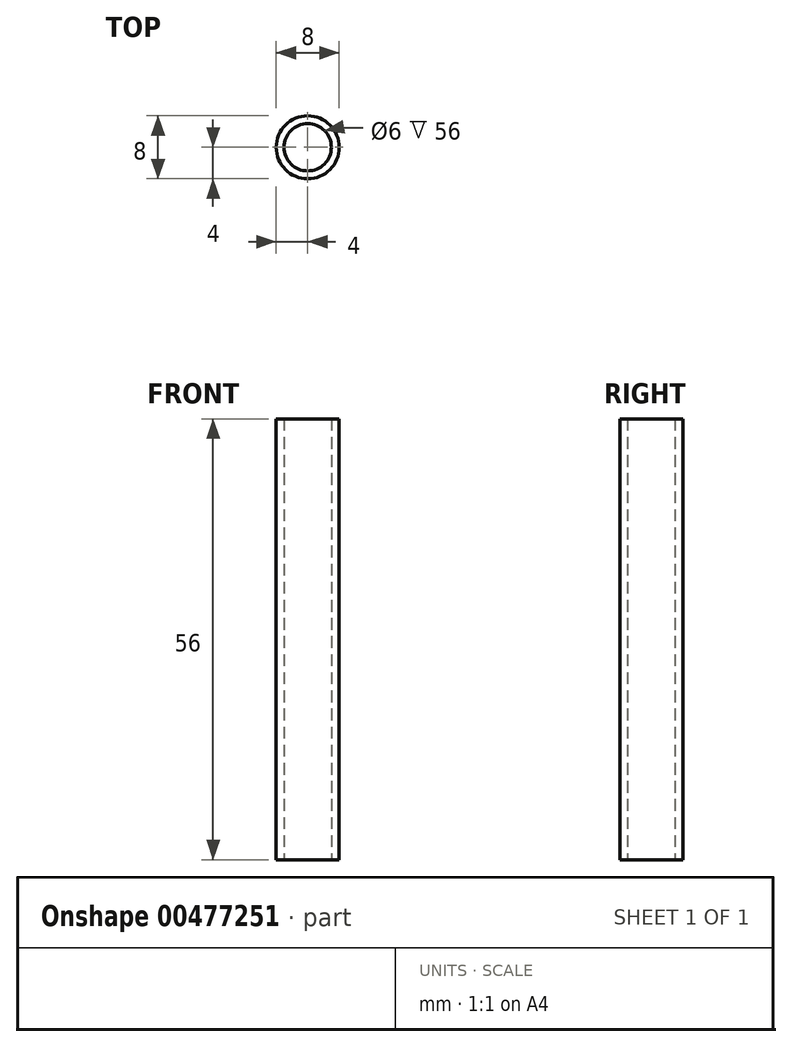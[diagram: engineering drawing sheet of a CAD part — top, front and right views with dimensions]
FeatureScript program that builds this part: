
annotation { "Feature Type Name" : "Feature", "Feature Type Description" : "" }
export const myFeature = defineFeature(function(context is Context, id is Id, definition is map)
    precondition{}
    {
        {
            var Q0;
            Q0=qCreatedBy(makeId("Top.planeOp"),FACE);
            var sketch = newSketch(context, id + "F0", { "sketchPlane" : qUnion([Q0])});
            skCircle(sketch, "E0", {"center": v(0, 0) * mm, "radius": 4 * mm});
            skCircle(sketch, "E1", {"center": v(0, 0) * mm, "radius": 3 * mm});
            skSolve(sketch);
        }
        {
            var Q0;
            Q0=makeQuery(id+"F0.imprint","IMPRINT",FACE,{"disambiguationData":[TD([[makeQuery(id+"F0.imprint","IMPRINT",EDGE,{"derivedFrom":sQuery(id+"F0.wireOp",EDGE,"E0")}),1.0]])]});
            extrude(context, id + "F1", {"entities" : qUnion([Q0]), "depth" : 56 * mm});
        }
    });
